# Revit family: Kabelrinne SKS-SKS 620_FT_FS_A2_A4_FSK_FTSO
name_source: partatom
category: Generic Models
revit_build: Autodesk Revit 2017 (Build: 20190508_0315(x64)
units: mm (PartAtom-declared; Revit-internal decimal feet)

## family parameters
Always vertical = Yes
Can host rebar = No
Cut with Voids When Loaded = No
Part Type = Normal
Room Calculation Point = No
Round Connector Dimension = Use Diameter
Shared = No
Work Plane-Based = No

## types (6) — shared parameters
Cut's number = 2
Cut's number 2 = 60
Cut's number 3 = 59
Cut's space = 50 mm  [stored 0.164042 ft]
Height = 51 mm
Length = 3000 mm  [stored 9.84252 ft]
Manufacturer = OBO BETTERMANN
URL = http:/www.obo-bettermann.com

## per-type parameters (varying)
| type | GTIN | Manufacturer Art.No. | Material | Width | Width 1 |
| SKS 615 FS | 4012196389711 | 6056156 | Strip-galvanised | 150 mm  [stored 0.492126 ft] | 75 mm |
| SKS 615 FT | 4012196390014 | 6056644 | hot-dip galvanised | 200 mm  [stored 0.656168 ft] | 100 mm  [stored 0.328084 ft] |
| SKS 620 A2 | 4012196120611 | 6056737 | Stainless Steel A2 | 200 mm  [stored 0.656168 ft] | 100 mm  [stored 0.328084 ft] |
| SKS 620 A4 | 4012196044887 | 6056755 | hot-dip galvanised | 200 mm  [stored 0.656168 ft] | 100 mm  [stored 0.328084 ft] |
| SKS 620 FT SO | 4012196147199 | 7190128 | hot-dip galvanised | 200 mm  [stored 0.656168 ft] | 100 mm  [stored 0.328084 ft] |
| SKS 620 FSK TGN | 4012195776345 | 6056204 | Polyester / epoxy | 200 mm  [stored 0.656168 ft] | 100 mm  [stored 0.328084 ft] |

note: column(s) folded — value = type name in every type: Article Type

note: [stored X ft] marks values corroborated as IEEE doubles in the binary element streams (Revit-internal decimal feet)

## geometry (parser evidence)
native form markers: Sweep x2
no freeform markers — native parametric forms only
